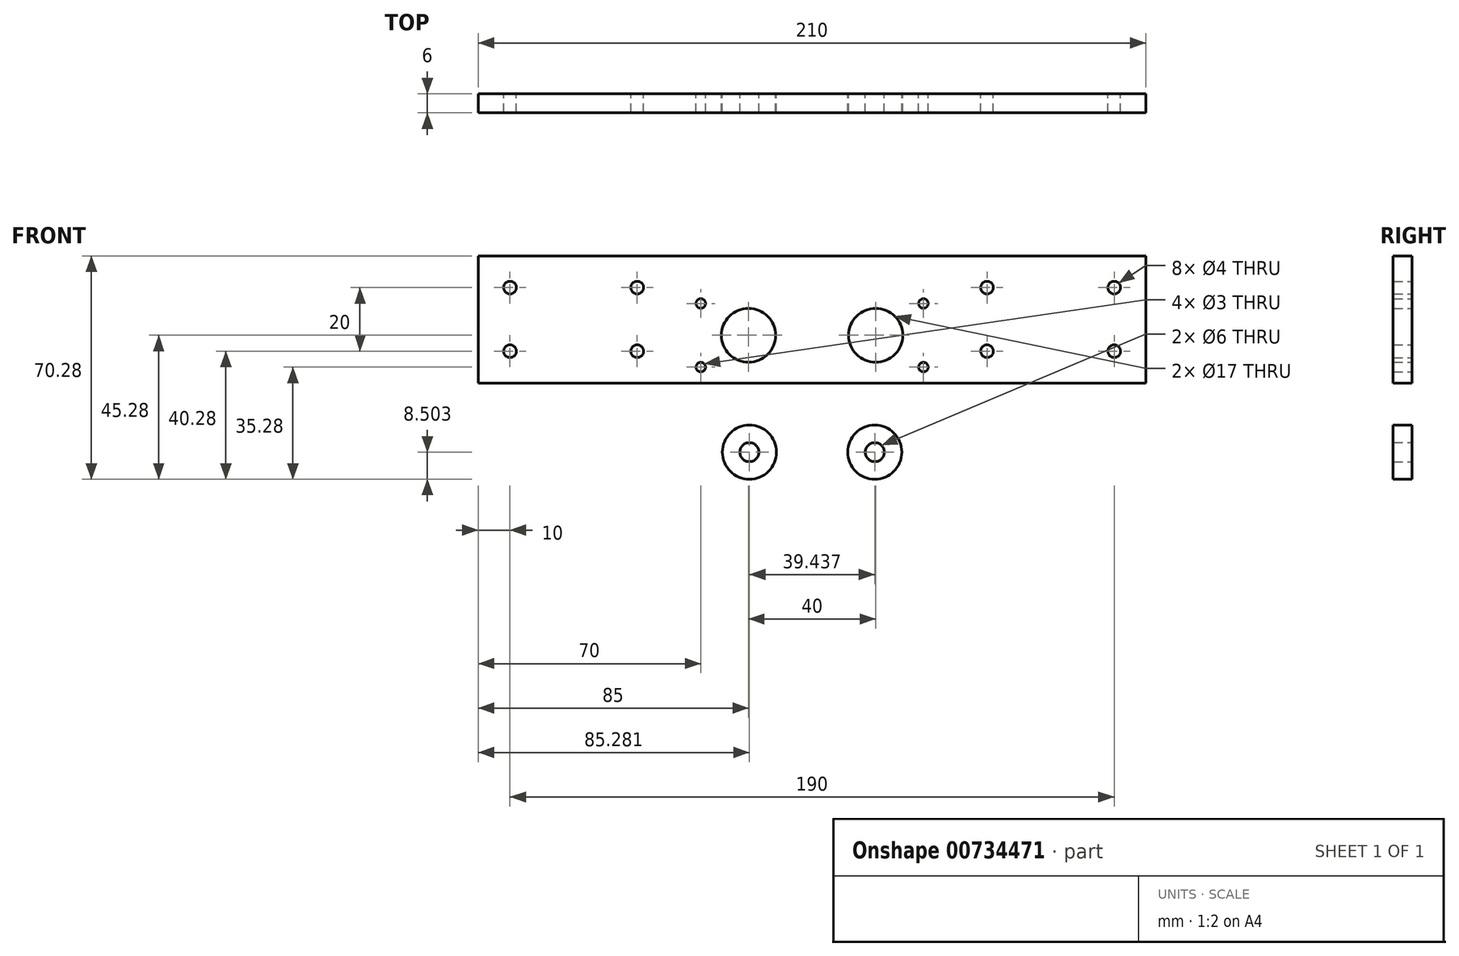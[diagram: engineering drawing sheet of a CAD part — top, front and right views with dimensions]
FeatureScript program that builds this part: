
annotation { "Feature Type Name" : "Feature", "Feature Type Description" : "" }
export const myFeature = defineFeature(function(context is Context, id is Id, definition is map)
    precondition{}
    {
        {
            var Q0;
            Q0=qCreatedBy(makeId("Front.planeOp"),FACE);
            var sketch = newSketch(context, id + "F0", { "sketchPlane" : qUnion([Q0])});
            skLineSegment(sketch, "E0.bottom", {"start": v(-105, 20) * mm, "end": v(105, 20) * mm});
            skLineSegment(sketch, "E0.top", {"start": v(-105, -20) * mm, "end": v(105, -20) * mm});
            skLineSegment(sketch, "E0.left", {"start": v(-105, 20) * mm, "end": v(-105, -20) * mm});
            skLineSegment(sketch, "E0.right", {"start": v(105, 20) * mm, "end": v(105, -20) * mm});
            skLineSegment(sketch, "E1", {"start": v(-194.37, 0) * mm, "end": v(228.5, 0) * mm, "construction": true});
            skCircle(sketch, "E2", {"center": v(95, 10) * mm, "radius": 2 * mm});
            skLineSegment(sketch, "E3", {"start": v(20, 25.69) * mm, "end": v(20, -38.98) * mm, "construction": true});
            skCircle(sketch, "E4", {"center": v(20, -5) * mm, "radius": 8.5 * mm});
            skCircle(sketch, "E5.MirrorC", {"center": v(95, -10) * mm, "radius": 2 * mm});
            skLineSegment(sketch, "E6.MirrorCS", {"start": v(20, -25.69) * mm, "end": v(20, 38.98) * mm, "construction": true});
            skCircle(sketch, "E7.MirrorC", {"center": v(-55, 10) * mm, "radius": 2 * mm});
            skCircle(sketch, "E8.MirrorC", {"center": v(-55, -10) * mm, "radius": 2 * mm});
            skLineSegment(sketch, "E9", {"start": v(0, 51.1) * mm, "end": v(0, -53.72) * mm, "construction": true});
            skCircle(sketch, "E10.MirrorC", {"center": v(-20, -5) * mm, "radius": 8.5 * mm});
            skLineSegment(sketch, "E11", {"start": v(75, 51.1) * mm, "end": v(75, -53.15) * mm, "construction": true});
            skCircle(sketch, "E12.MirrorC", {"center": v(55, 10) * mm, "radius": 2 * mm});
            skCircle(sketch, "E13.MirrorC", {"center": v(55, -10) * mm, "radius": 2 * mm});
            skLineSegment(sketch, "E14", {"start": v(-20, 39.17) * mm, "end": v(-20, -45.08) * mm, "construction": true});
            skCircle(sketch, "E15.MirrorC", {"center": v(-95, 10) * mm, "radius": 2 * mm});
            skCircle(sketch, "E16.MirrorC", {"center": v(-95, -10) * mm, "radius": 2 * mm});
            skLineSegment(sketch, "E17", {"start": v(-48.56, -5) * mm, "end": v(51.2, -5) * mm, "construction": true});
            skCircle(sketch, "E18", {"center": v(-35, 5) * mm, "radius": 1.5 * mm});
            skCircle(sketch, "E19", {"center": v(-35, -15) * mm, "radius": 1.5 * mm});
            skCircle(sketch, "E20", {"center": v(35, 5) * mm, "radius": 1.5 * mm});
            skCircle(sketch, "E21", {"center": v(35, -15) * mm, "radius": 1.5 * mm});
            skSolve(sketch);
        }
        {
            var Q0;
            Q0 = qSketchRegion(id + "F0", true);
            extrude(context, id + "F1", {"entities" : qUnion([Q0]), "depth" : 6 * mm, "offsetDistance" : 25 * mm});
        }
        {
            var Q0;
            Q0=qCreatedBy(makeId("Front.planeOp"),FACE);
            var sketch = newSketch(context, id + "F2", { "sketchPlane" : qUnion([Q0])});
            skCircle(sketch, "E22", {"center": v(-19.72, -41.78) * mm, "radius": 8.5 * mm});
            skCircle(sketch, "E23", {"center": v(-19.72, -41.78) * mm, "radius": 3 * mm});
            skCircle(sketch, "E24.MirrorC", {"center": v(19.72, -41.78) * mm, "radius": 8.5 * mm});
            skCircle(sketch, "E25.MirrorC", {"center": v(19.72, -41.78) * mm, "radius": 3 * mm});
            skSolve(sketch);
        }
        {
            var Q0;
            Q0 = qSketchRegion(id + "F2", true);
            extrude(context, id + "F3", {"entities" : qUnion([Q0]), "depth" : 6 * mm, "offsetDistance" : 25 * mm});
        }
    });
